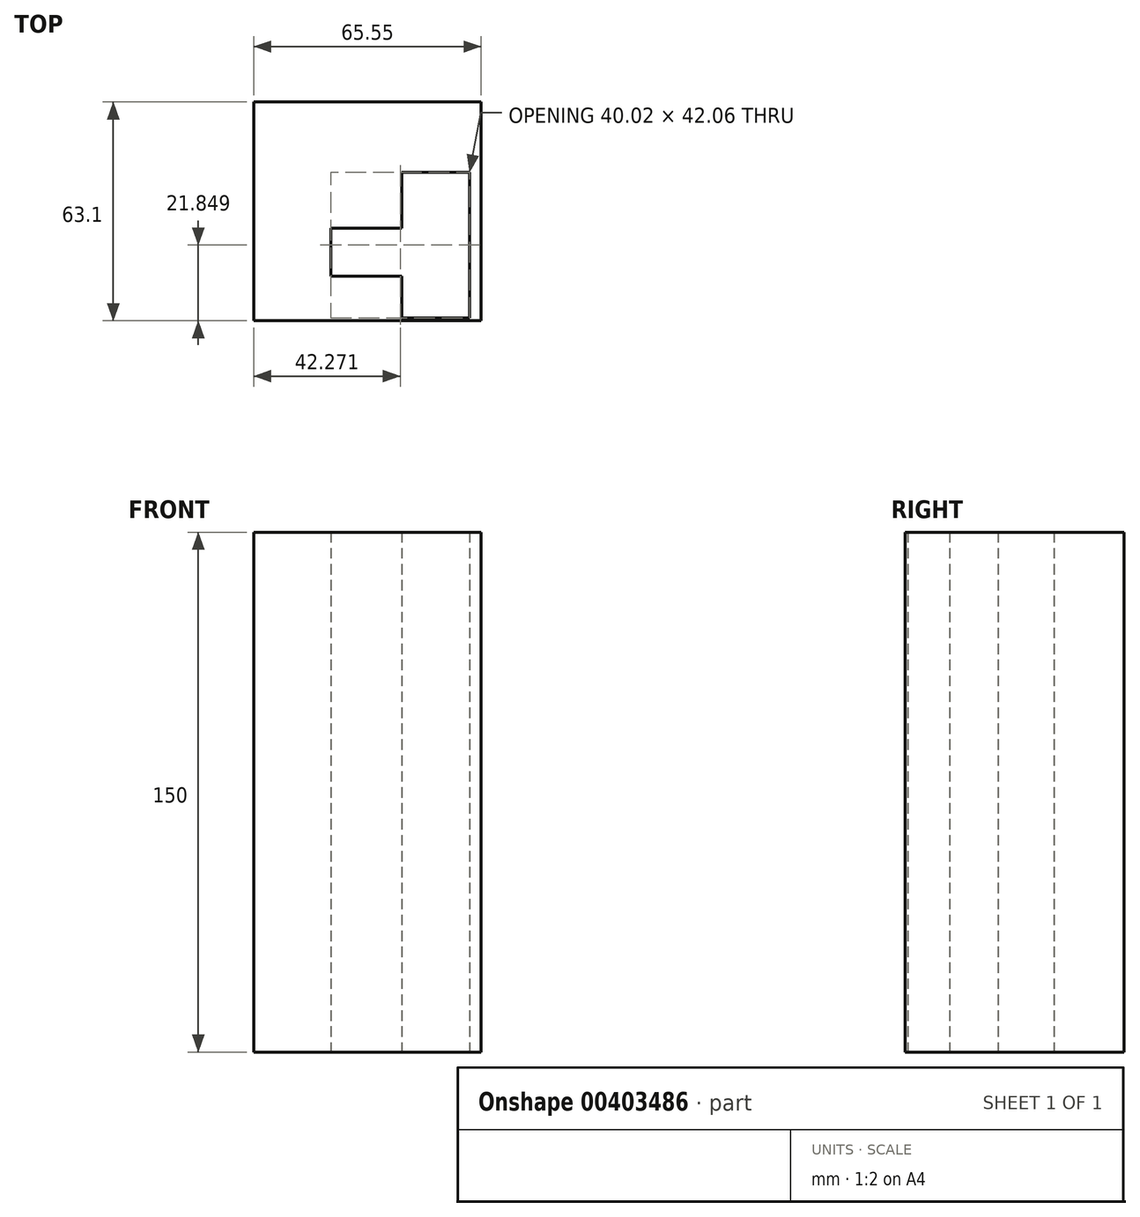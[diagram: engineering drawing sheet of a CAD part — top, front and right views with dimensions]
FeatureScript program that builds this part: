
annotation { "Feature Type Name" : "Feature", "Feature Type Description" : "" }
export const myFeature = defineFeature(function(context is Context, id is Id, definition is map)
    precondition{}
    {
        {
            var Q0;
            Q0=qCreatedBy(makeId("Top.planeOp"),FACE);
            var sketch = newSketch(context, id + "F0", { "sketchPlane" : qUnion([Q0])});
            skLineSegment(sketch, "E0.bottom", {"start": v(28.38, -13.88) * mm, "end": v(0, -13.88) * mm});
            skLineSegment(sketch, "E0.top", {"start": v(28.38, 0) * mm, "end": v(0, 0) * mm});
            skLineSegment(sketch, "E0.left", {"start": v(28.38, -13.88) * mm, "end": v(28.38, 0) * mm});
            skLineSegment(sketch, "E0.right", {"start": v(0, -13.88) * mm, "end": v(0, 0) * mm});
            skLineSegment(sketch, "E1.bottom", {"start": v(20.42, 16.13) * mm, "end": v(40.02, 16.13) * mm});
            skLineSegment(sketch, "E1.top", {"start": v(20.42, -25.93) * mm, "end": v(40.02, -25.93) * mm});
            skLineSegment(sketch, "E1.left", {"start": v(20.42, 16.13) * mm, "end": v(20.42, -25.93) * mm});
            skLineSegment(sketch, "E1.right", {"start": v(40.02, 16.13) * mm, "end": v(40.02, -25.93) * mm});
            skLineSegment(sketch, "E2.bottom", {"start": v(43.29, 36.35) * mm, "end": v(-22.26, 36.35) * mm});
            skLineSegment(sketch, "E2.top", {"start": v(43.29, -26.75) * mm, "end": v(-22.26, -26.75) * mm});
            skLineSegment(sketch, "E2.left", {"start": v(43.29, 36.35) * mm, "end": v(43.29, -26.75) * mm});
            skLineSegment(sketch, "E2.right", {"start": v(-22.26, 36.35) * mm, "end": v(-22.26, -26.75) * mm});
            skSolve(sketch);
        }
        {
            var Q0;
            Q0 = qSketchRegion(id + "F0", true);
            extrude(context, id + "F1", {"entities" : qUnion([Q0]), "depth" : 150 * mm});
        }
    });
